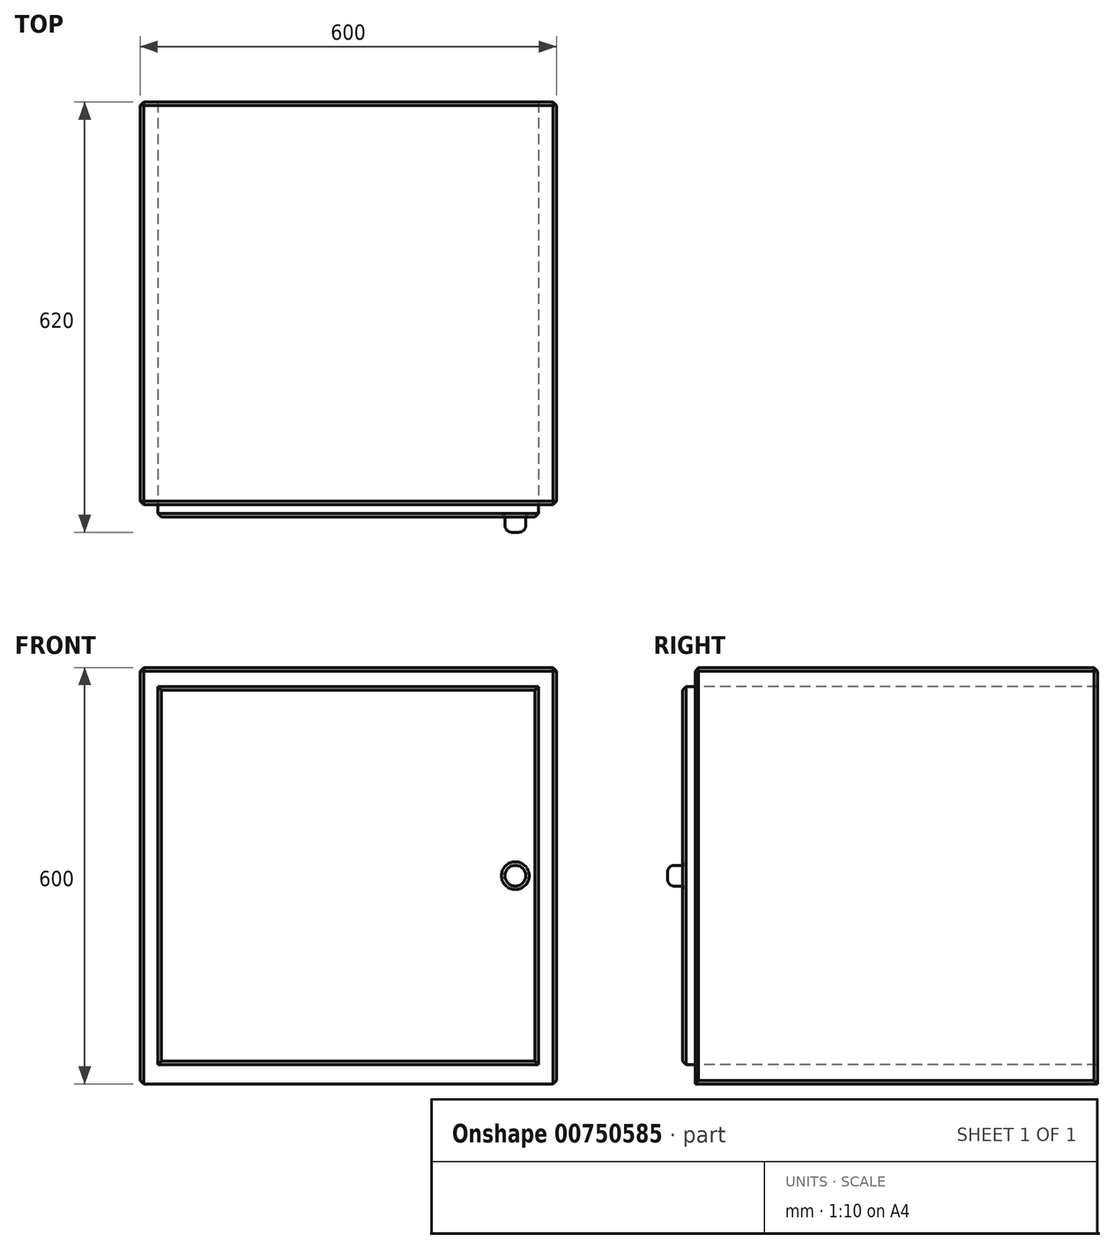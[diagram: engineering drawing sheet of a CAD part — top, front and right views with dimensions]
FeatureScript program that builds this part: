
annotation { "Feature Type Name" : "Feature", "Feature Type Description" : "" }
export const myFeature = defineFeature(function(context is Context, id is Id, definition is map)
    precondition{}
    {
        {
            var Q0;
            Q0=qCreatedBy(makeId("Front.planeOp"),FACE);
            var sketch = newSketch(context, id + "F0", { "sketchPlane" : qUnion([Q0])});
            skLineSegment(sketch, "E0.bottom", {"start": v(-300, 300) * mm, "end": v(300, 300) * mm});
            skLineSegment(sketch, "E0.top", {"start": v(-300, -300) * mm, "end": v(300, -300) * mm});
            skLineSegment(sketch, "E0.left", {"start": v(-300, 300) * mm, "end": v(-300, -300) * mm});
            skLineSegment(sketch, "E0.right", {"start": v(300, 300) * mm, "end": v(300, -300) * mm});
            skPoint(sketch, "E0.middle", {"position": v(0, 0) * mm});
            skLineSegment(sketch, "E1.bottom", {"start": v(-274.13, 272.52) * mm, "end": v(274.13, 272.52) * mm});
            skLineSegment(sketch, "E1.top", {"start": v(-274.13, -272.52) * mm, "end": v(274.13, -272.52) * mm});
            skLineSegment(sketch, "E1.left", {"start": v(-274.13, 272.52) * mm, "end": v(-274.13, -272.52) * mm});
            skLineSegment(sketch, "E1.right", {"start": v(274.13, 272.52) * mm, "end": v(274.13, -272.52) * mm});
            skCircle(sketch, "E2", {"center": v(240.82, 0) * mm, "radius": 15 * mm});
            skSolve(sketch);
        }
        {
            var Q0;
            Q0=makeQuery(id+"F0.imprint","IMPRINT",FACE,{"disambiguationData":[TD([[makeQuery(id+"F0.imprint","IMPRINT",EDGE,{"derivedFrom":sQuery(id+"F0.wireOp",EDGE,"E0.bottom")}),-1.0]])]});
            extrude(context, id + "F1", {"entities" : qUnion([Q0]), "oppositeDirection" : true, "depth" : 550 * mm, "offsetDistance" : 25 * mm});
        }
        {
            var Q0;
            Q0=makeQuery(id+"F1.opExtrude","CAP_FACE",FACE,{"disambiguationData":[OSD([sQuery(id+"F0.wireOp",EDGE,"E0.bottom"),sQuery(id+"F0.wireOp",EDGE,"E0.top"),sQuery(id+"F0.wireOp",EDGE,"E0.left"),sQuery(id+"F0.wireOp",EDGE,"E0.right"),sQuery(id+"F0.wireOp",EDGE,"E1.bottom"),sQuery(id+"F0.wireOp",EDGE,"E1.top"),sQuery(id+"F0.wireOp",EDGE,"E1.left"),sQuery(id+"F0.wireOp",EDGE,"E1.right")])],"isStart":false});
            var Q1;
            Q1=sQuery(id+"F0.wireOp",EDGE,"E2");
            extrude(context, id + "F2", {"entities" : qUnion([Q0]), "operationType" : NewBodyOperationType.ADD, "surfaceEntities" : qUnion([Q1]), "depth" : 30 * mm, "offsetDistance" : 25 * mm});
        }
        {
            var Q0;
            Q0=makeQuery(id+"F0.imprint","IMPRINT",FACE,{"disambiguationData":[TD([[makeQuery(id+"F0.imprint","IMPRINT",EDGE,{"derivedFrom":sQuery(id+"F0.wireOp",EDGE,"E1.bottom")}),-1.0]])]});
            extrude(context, id + "F3", {"entities" : qUnion([Q0]), "depth" : 18 * mm, "offsetDistance" : 25 * mm});
        }
        {
            var Q0;
            {var subQ0=sQuery(id+"F0.wireOp",EDGE,"E0.left");Q0=makeQuery(id+"F2.boolean.opBoolean","MERGE",FACE,{"derivedFrom":[makeQuery(id+"F1.opExtrude","SWEPT_FACE",FACE,{"disambiguationData":[OSD([subQ0])]}),makeQuery(id+"F2.opExtrude","SWEPT_FACE",FACE,{"disambiguationData":[OSD([subQ0])]})]});}
            var Q1;
            {var subQ0=sQuery(id+"F0.wireOp",EDGE,"E0.bottom");Q1=makeQuery(id+"F2.boolean.opBoolean","MERGE",FACE,{"derivedFrom":[makeQuery(id+"F1.opExtrude","SWEPT_FACE",FACE,{"disambiguationData":[OSD([subQ0])]}),makeQuery(id+"F2.opExtrude","SWEPT_FACE",FACE,{"disambiguationData":[OSD([subQ0])]})]});}
            var Q2;
            {var subQ0=sQuery(id+"F0.wireOp",EDGE,"E0.right");Q2=makeQuery(id+"F2.boolean.opBoolean","MERGE",FACE,{"derivedFrom":[makeQuery(id+"F1.opExtrude","SWEPT_FACE",FACE,{"disambiguationData":[OSD([subQ0])]}),makeQuery(id+"F2.opExtrude","SWEPT_FACE",FACE,{"disambiguationData":[OSD([subQ0])]})]});}
            var Q3;
            Q3=makeQuery(id+"F3.opExtrude","CAP_FACE",FACE,{"disambiguationData":[OSD([sQuery(id+"F0.wireOp",EDGE,"E1.bottom"),sQuery(id+"F0.wireOp",EDGE,"E1.top"),sQuery(id+"F0.wireOp",EDGE,"E1.left"),sQuery(id+"F0.wireOp",EDGE,"E1.right"),sQuery(id+"F0.wireOp",EDGE,"E2")])],"isStart":false});
            chamfer(context, id + "F4", {"entities" : qUnion([Q0, Q1, Q2, Q3]), "width" : 5 * mm, "tangentPropagation" : true});
        }
        {
            var Q0;
            Q0=makeQuery(id+"F0.imprint","IMPRINT",FACE,{"disambiguationData":[TD([[makeQuery(id+"F0.imprint","IMPRINT",EDGE,{"derivedFrom":sQuery(id+"F0.wireOp",EDGE,"E2")}),1.0]])]});
            var Q1;
            Q1=sQuery(id+"F0.wireOp",EDGE,"E2");
            extrude(context, id + "F5", {"entities" : qUnion([Q0]), "operationType" : NewBodyOperationType.ADD, "surfaceEntities" : qUnion([Q1]), "depth" : 40 * mm, "offsetDistance" : 25 * mm});
        }
        {
            var Q0;
            Q0=makeQuery(id+"F5.opExtrude","CAP_FACE",FACE,{"disambiguationData":[OSD([sQuery(id+"F0.wireOp",EDGE,"E2")])],"isStart":false});
            fillet(context, id + "F6", {"entities" : qUnion([Q0]), "radius" : 10 * mm, "tangentPropagation" : true, "allowEdgeOverflow" : false});
        }
    });
